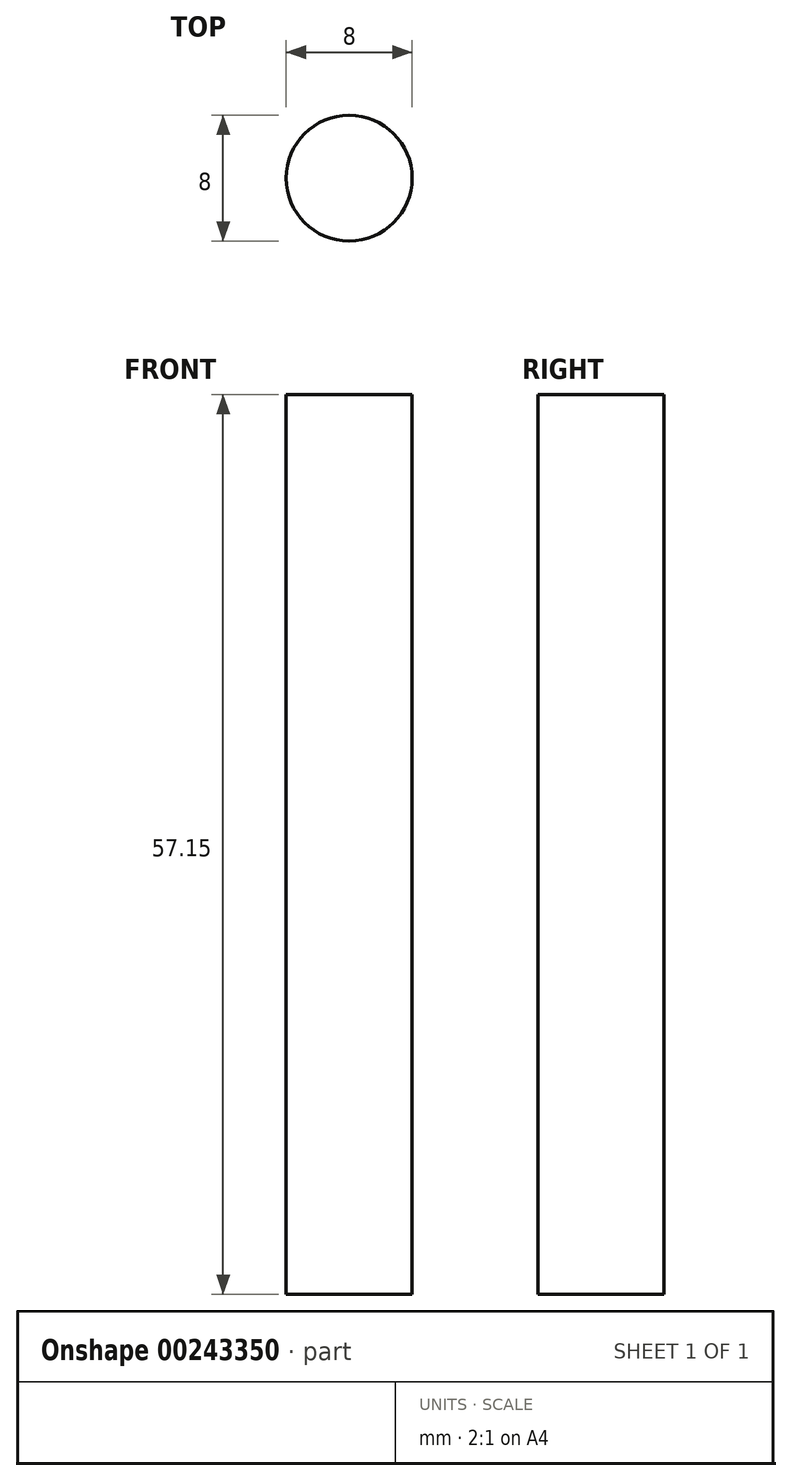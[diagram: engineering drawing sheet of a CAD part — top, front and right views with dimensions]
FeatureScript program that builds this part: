
annotation { "Feature Type Name" : "Feature", "Feature Type Description" : "" }
export const myFeature = defineFeature(function(context is Context, id is Id, definition is map)
    precondition{}
    {
        {
            var Q0;
            Q0=qCreatedBy(makeId("Top.planeOp"),FACE);
            var sketch = newSketch(context, id + "F0", { "sketchPlane" : qUnion([Q0])});
            skCircle(sketch, "E0", {"center": v(0, 0) * mm, "radius": 4 * mm});
            skSolve(sketch);
        }
        {
            var Q0;
            Q0 = qSketchRegion(id + "F0", true);
            extrude(context, id + "F1", {"entities" : qUnion([Q0]), "depth" : 57.15 * mm});
        }
    });
